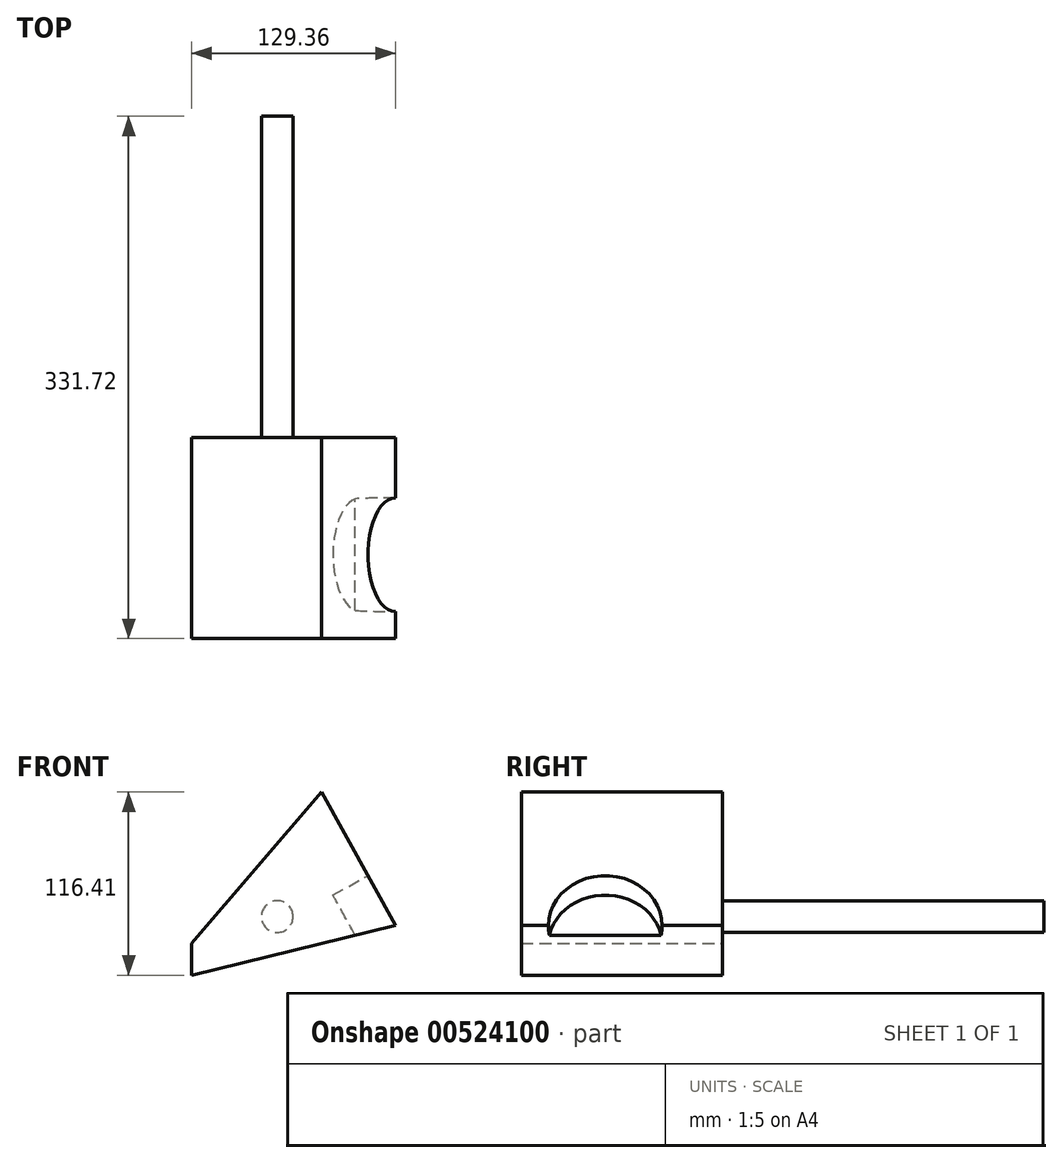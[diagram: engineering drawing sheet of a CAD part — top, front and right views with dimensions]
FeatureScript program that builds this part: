
annotation { "Feature Type Name" : "Feature", "Feature Type Description" : "" }
export const myFeature = defineFeature(function(context is Context, id is Id, definition is map)
    precondition{}
    {
        {
            var Q0;
            Q0=qCreatedBy(makeId("Front.planeOp"),FACE);
            var sketch = newSketch(context, id + "F0", { "sketchPlane" : qUnion([Q0])});
            skLineSegment(sketch, "E0", {"start": v(-54.32, 89.04) * mm, "end": v(-54.32, 68.83) * mm});
            skLineSegment(sketch, "E1", {"start": v(-54.32, 68.83) * mm, "end": v(75.04, 100.4) * mm});
            skLineSegment(sketch, "E2", {"start": v(75.04, 100.4) * mm, "end": v(28.23, 185.24) * mm});
            skLineSegment(sketch, "E3", {"start": v(28.23, 185.24) * mm, "end": v(-54.32, 89.04) * mm});
            skSolve(sketch);
        }
        {
            var Q0;
            Q0=makeQuery(id+"F0.imprint","IMPRINT",FACE,{"disambiguationData":[TD([[makeQuery(id+"F0.imprint","IMPRINT",EDGE,{"derivedFrom":sQuery(id+"F0.wireOp",EDGE,"E0")}),1.0]])]});
            extrude(context, id + "F1", {"entities" : qUnion([Q0]), "depth" : 127.68 * mm, "offsetDistance" : 25.4 * mm});
        }
        {
            var Q0;
            Q0=makeQuery(id+"F1.opExtrude","CAP_FACE",FACE,{"disambiguationData":[OSD([sQuery(id+"F0.wireOp",EDGE,"E0"),sQuery(id+"F0.wireOp",EDGE,"E1"),sQuery(id+"F0.wireOp",EDGE,"E2"),sQuery(id+"F0.wireOp",EDGE,"E3")])],"isStart":true});
            var sketch = newSketch(context, id + "F2", { "sketchPlane" : qUnion([Q0])});
            skCircle(sketch, "E4", {"center": v(0, 106.1) * mm, "radius": 10.06 * mm});
            skSolve(sketch);
        }
        {
            var Q0;
            Q0=makeQuery(id+"F2.imprint","IMPRINT",FACE,{"disambiguationData":[TD([[makeQuery(id+"F2.imprint","IMPRINT",EDGE,{"derivedFrom":sQuery(id+"F2.wireOp",EDGE,"E4")}),1.0]])]});
            extrude(context, id + "F3", {"entities" : qUnion([Q0]), "operationType" : NewBodyOperationType.ADD, "depth" : 204.04 * mm, "offsetDistance" : 25.4 * mm});
        }
        {
            var Q0;
            Q0=makeQuery(id+"F1.opExtrude","SWEPT_FACE",FACE,{"disambiguationData":[OSD([sQuery(id+"F0.wireOp",EDGE,"E2")])]});
            var sketch = newSketch(context, id + "F4", { "sketchPlane" : qUnion([Q0])});
            skCircle(sketch, "E5", {"center": v(-74.42, 51.66) * mm, "radius": 36.13 * mm});
            skSolve(sketch);
        }
        {
            var Q0;
            Q0 = qSketchRegion(id + "F4", true);
            extrude(context, id + "F5", {"entities" : qUnion([Q0]), "operationType" : NewBodyOperationType.REMOVE, "oppositeDirection" : true, "depth" : 25.4 * mm, "offsetDistance" : 25.4 * mm});
        }
    });
